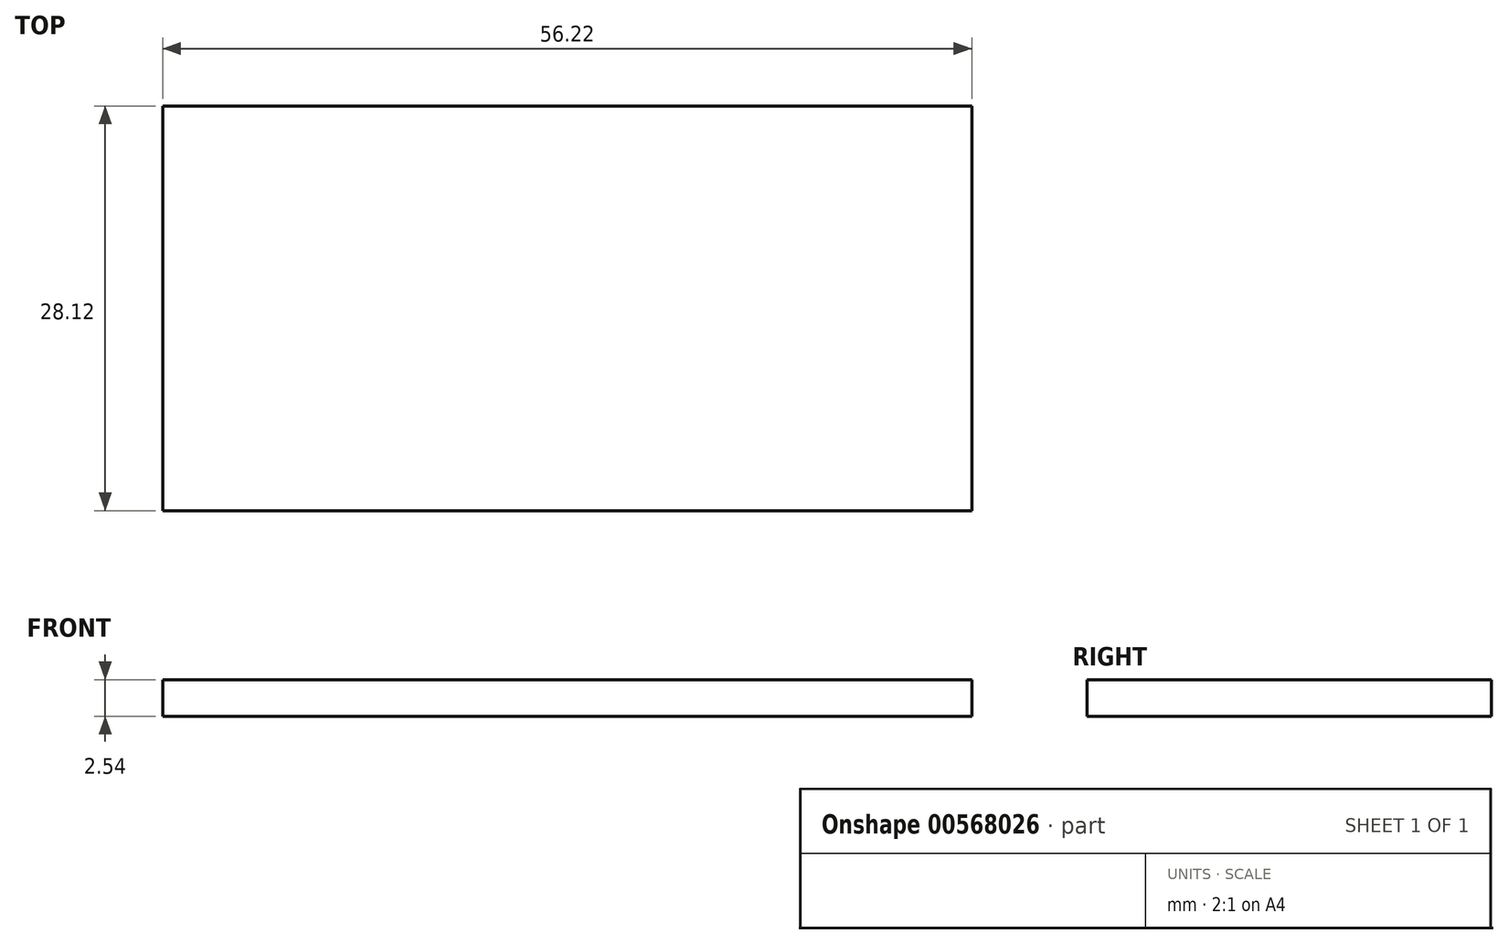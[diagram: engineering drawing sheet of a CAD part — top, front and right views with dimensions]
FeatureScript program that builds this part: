
annotation { "Feature Type Name" : "Feature", "Feature Type Description" : "" }
export const myFeature = defineFeature(function(context is Context, id is Id, definition is map)
    precondition{}
    {
        {
            var Q0;
            Q0=qCreatedBy(makeId("Top.planeOp"),FACE);
            var sketch = newSketch(context, id + "F0", { "sketchPlane" : qUnion([Q0])});
            skLineSegment(sketch, "E0.bottom", {"start": v(-28.11, 14.06) * mm, "end": v(28.11, 14.06) * mm});
            skLineSegment(sketch, "E0.top", {"start": v(-28.11, -14.06) * mm, "end": v(28.11, -14.06) * mm});
            skLineSegment(sketch, "E0.left", {"start": v(-28.11, 14.06) * mm, "end": v(-28.11, -14.06) * mm});
            skLineSegment(sketch, "E0.right", {"start": v(28.11, 14.06) * mm, "end": v(28.11, -14.06) * mm});
            skPoint(sketch, "E0.middle", {"position": v(0, 0) * mm});
            skSolve(sketch);
        }
        {
            var Q0;
            Q0 = qSketchRegion(id + "F0", true);
            extrude(context, id + "F1", {"entities" : qUnion([Q0]), "depth" : 2.54 * mm, "offsetDistance" : 25.4 * mm});
        }
    });
